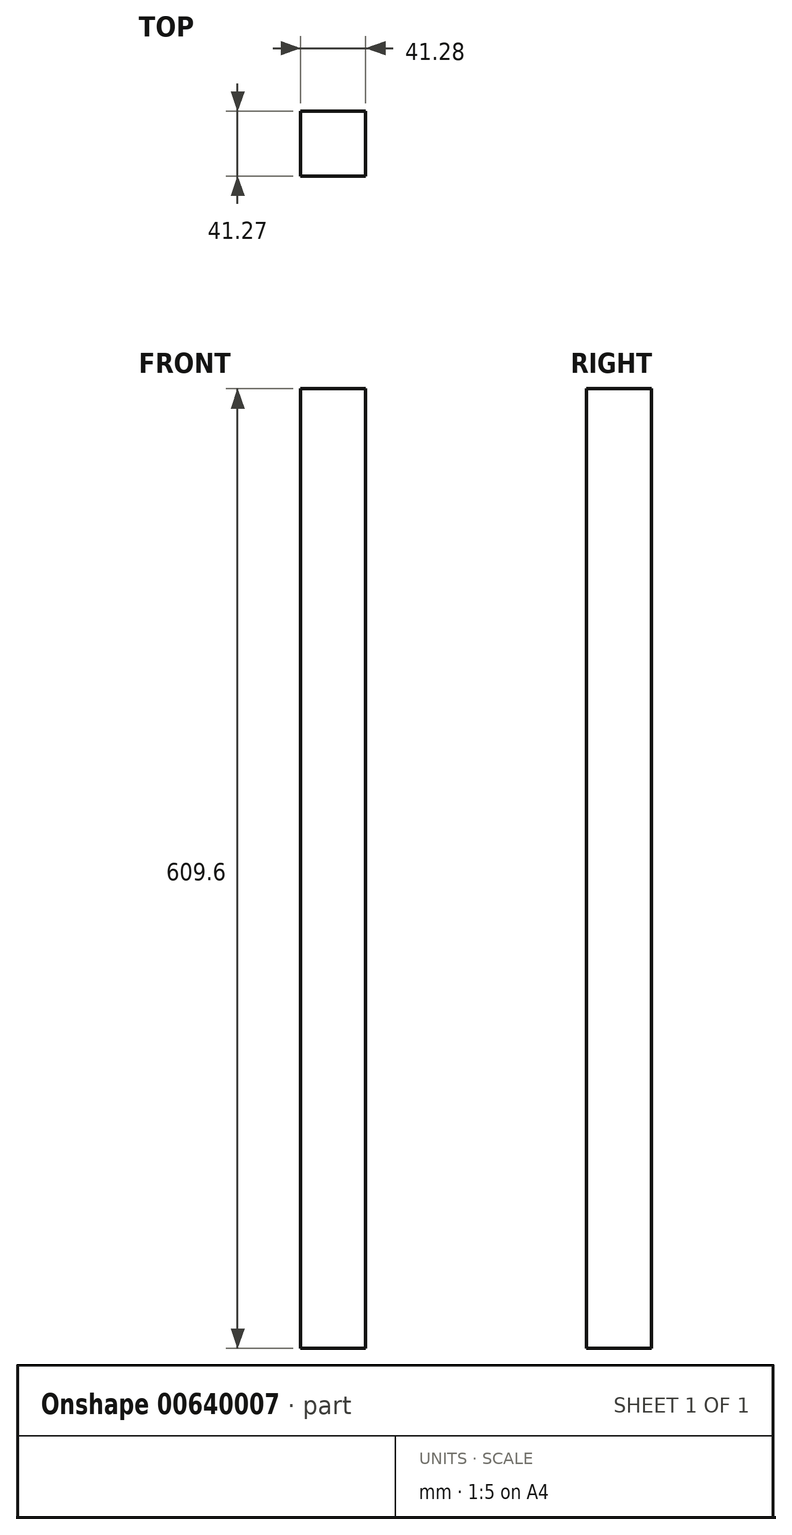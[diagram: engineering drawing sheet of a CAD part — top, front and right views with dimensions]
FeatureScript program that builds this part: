
annotation { "Feature Type Name" : "Feature", "Feature Type Description" : "" }
export const myFeature = defineFeature(function(context is Context, id is Id, definition is map)
    precondition{}
    {
        {
            var Q0;
            Q0=qCreatedBy(makeId("Front.planeOp"),FACE);
            var sketch = newSketch(context, id + "F0", { "sketchPlane" : qUnion([Q0])});
            skLineSegment(sketch, "E0.bottom", {"start": v(20.64, -304.8) * mm, "end": v(-20.64, -304.8) * mm});
            skLineSegment(sketch, "E0.top", {"start": v(20.64, 304.8) * mm, "end": v(-20.64, 304.8) * mm});
            skLineSegment(sketch, "E0.left", {"start": v(20.64, -304.8) * mm, "end": v(20.64, 304.8) * mm});
            skLineSegment(sketch, "E0.right", {"start": v(-20.64, -304.8) * mm, "end": v(-20.64, 304.8) * mm});
            skPoint(sketch, "E0.middle", {"position": v(0, 0) * mm});
            skSolve(sketch);
        }
        {
            var Q0;
            Q0=makeQuery(id+"F0.imprint","IMPRINT",FACE,{"disambiguationData":[TD([[makeQuery(id+"F0.imprint","IMPRINT",EDGE,{"derivedFrom":sQuery(id+"F0.wireOp",EDGE,"E0.bottom")}),-1.0]])]});
            extrude(context, id + "F1", {"entities" : qUnion([Q0]), "depth" : 41.27 * mm, "offsetDistance" : 25.4 * mm});
        }
    });
